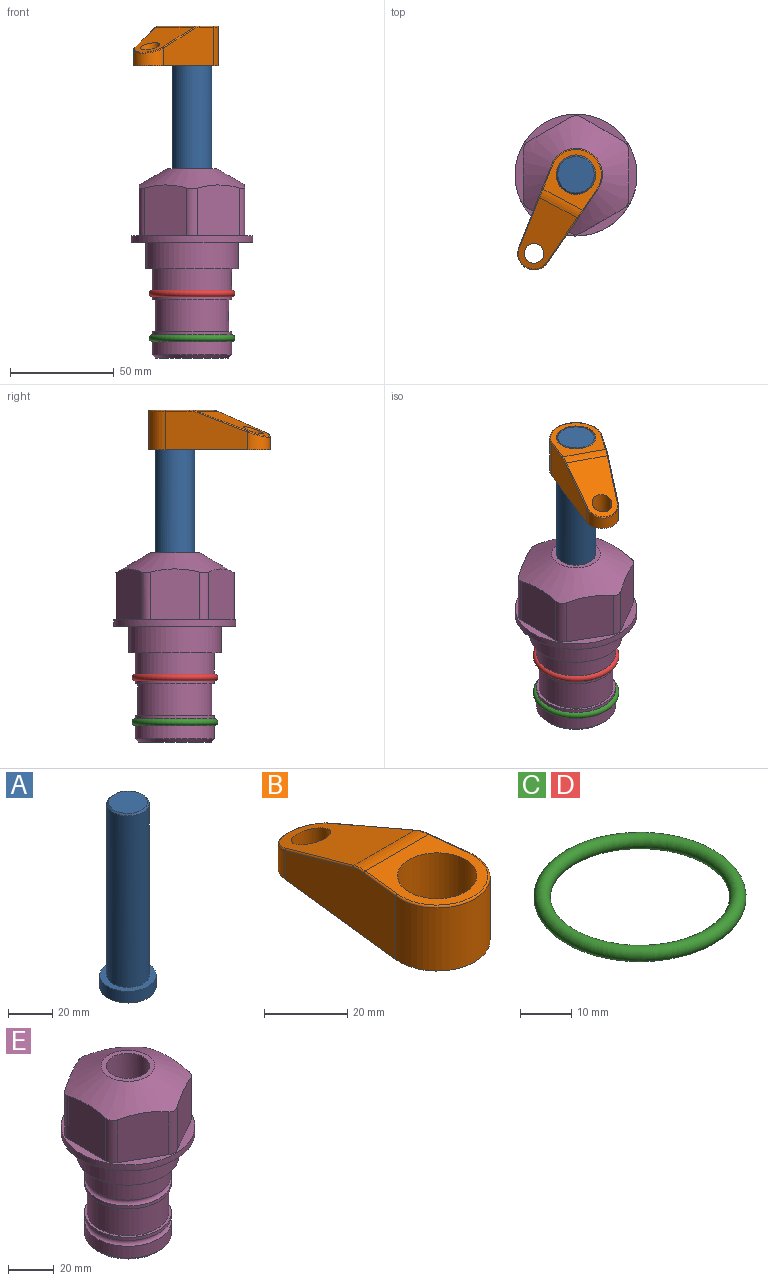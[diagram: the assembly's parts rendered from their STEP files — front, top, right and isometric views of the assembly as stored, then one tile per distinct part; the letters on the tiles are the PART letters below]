
ASSEMBLY  parts=5 mates=3
PART A: 6 faces, bbox 25.4x25.4x101.6 mm
  f0: plane 17.46x17.46mm, normal (0,0,1), area 239.5mm2, adj f5
  f1: plane 25.4x25.4mm, normal (0,0,-1), area 506.7mm2, adj f2
  f2: cylinder r=12.7mm len=25.4mm, axis (0,0,1), area 506.7mm2, adj f1,f3
  f3: plane 25.4x25.4mm, normal (0,0,1), area 221.7mm2, adj f2,f4
  f4: cylinder r=9.53mm len=94.46mm, axis (0,0,1), area 5653mm2, adj f3,f5
  f5: cone r=8.73mm half-angle=45deg, axis (0,0,-1), area 64.4mm2, adj f0,f4
PART B: 44 faces, bbox 27.5x64.5x19.1 mm
  f0: plane 2.3x0.95mm, normal (0,0,-1), area 1mm2, adj f25,f30,f34
  f1: plane 63.5x25.4mm, normal (0,0,-1), area 561.7mm2, adj f2,f3,f4,f5,f6,f7,f19,f20
  f2: cylinder r=12.7mm len=25.4mm, axis (0,0,-1), area 792.2mm2, adj f1,f3,f5,f13
  f3: plane 42.33x18.54mm, normal (0.99,0.11,0), area 647mm2, adj f1,f2,f4,f11,f12,f14
  f4: cylinder r=7.94mm len=15.78mm, axis (0,0,-1), area 158.6mm2, adj f1,f3,f5,f16
  f5: plane 42.33x18.54mm, normal (-0.99,0.11,0), area 647mm2, adj f1,f2,f4,f15,f17,f18
  f6: cylinder r=9.53mm len=19.05mm, axis (0,0,-1), area 1140.1mm2, adj f1,f8
  f7: cylinder r=4.76mm len=10.98mm, axis (0,0,-1), area 276.1mm2, adj f1,f9
  f8: plane 25.83x24.38mm, normal (0,0,1), area 262.2mm2, adj f6,f10,f11,f13,f15
  f9: plane 32.49x20.55mm, normal (0,0.34,0.94), area 489.9mm2, adj f7,f10,f14,f16,f18
  f10: cylinder r=12.7mm len=21.49mm, axis (-1,0,0), area 93.2mm2, adj f8,f9,f12,f17
  f11: cylinder r=0.51mm len=12.34mm, axis (0.11,-0.99,0), area 9.9mm2, adj f3,f8,f12,f13
  f12: bspline ~7.62x1.64mm, area 3.5mm2, adj f3,f10,f11,f14
  f13: torus R=12.19mm, axis (0,0,1), area 33.6mm2, adj f2,f8,f11,f15
  f14: cylinder r=0.51mm len=26.01mm, axis (0.1,-0.93,0.34), area 21.6mm2, adj f3,f9,f12,f16
  f15: cylinder r=0.51mm len=12.34mm, axis (0.11,0.99,0), area 9.9mm2, adj f5,f8,f13,f17
  f16: bspline ~15.78x7.05mm, area 15.7mm2, adj f4,f9,f14,f18
  f17: bspline ~7.62x1.64mm, area 3.5mm2, adj f5,f10,f15,f18
  f18: cylinder r=0.51mm len=26.01mm, axis (0.1,0.93,-0.34), area 21.6mm2, adj f5,f9,f16,f17
  f19: plane 21.6x14.29mm, normal (-0.99,-0.11,0), area 242.6mm2, adj f1,f26,f28,f34,f36,f38
  f20: plane 21.6x14.29mm, normal (0.99,-0.11,0), area 242.6mm2, adj f1,f27,f29,f37,f39,f41
  f21: cylinder r=12.7mm len=14.29mm, axis (0,0,-1), area 173.2mm2, adj f1,f26,f27,f30,f31,f33
  f22: cylinder r=7.94mm len=7.63mm, axis (0,0,-1), area 53.8mm2, adj f1,f28,f29,f42
  f23: plane 2.3x0.95mm, normal (0,0,-1), area 1mm2, adj f25,f33,f37
  f24: plane 17.94x12.32mm, normal (0,-0.34,-0.94), area 191.2mm2, adj f25,f38,f41,f42
  f25: cylinder r=9.53mm len=12.93mm, axis (-1,0,0), area 37.5mm2, adj f0,f23,f24,f31,f36,f39
  f26: cylinder r=1.59mm len=14.29mm, axis (0,0,-1), area 49mm2, adj f1,f19,f21,f32
  f27: cylinder r=1.59mm len=14.29mm, axis (0,0,-1), area 49mm2, adj f1,f20,f21,f35
  f28: cylinder r=1.59mm len=7.28mm, axis (0,0,-1), area 22.1mm2, adj f1,f19,f22,f40
  f29: cylinder r=1.59mm len=7.28mm, axis (0,0,-1), area 22.1mm2, adj f1,f20,f22,f43
  f30: torus R=14.29mm, axis (0,0,1), area 5.8mm2, adj f0,f21,f31,f32
  f31: bspline ~11.06x2.73mm, area 20.8mm2, adj f21,f25,f30,f33
  f32: sphere r=1.59mm, area 5.4mm2, adj f26,f30,f34
  f33: torus R=14.29mm, axis (0,0,1), area 5.8mm2, adj f21,f23,f31,f35
  f34: cylinder r=1.59mm len=1.68mm, axis (-0.11,0.99,0), area 2.4mm2, adj f0,f19,f32,f36
  f35: sphere r=1.59mm, area 5.4mm2, adj f27,f33,f37
  f36: bspline ~5.82x2.33mm, area 7.7mm2, adj f19,f25,f34,f38
  f37: cylinder r=1.59mm len=1.68mm, axis (0.11,0.99,0), area 2.4mm2, adj f20,f23,f35,f39
  f38: cylinder r=1.59mm len=18.33mm, axis (0.1,-0.93,0.34), area 46.7mm2, adj f19,f24,f36,f40
  f39: bspline ~5.82x2.33mm, area 7.7mm2, adj f20,f25,f37,f41
  f40: sphere r=1.59mm, area 3.6mm2, adj f28,f38,f42
  f41: cylinder r=1.59mm len=18.33mm, axis (0.1,0.93,-0.34), area 46.7mm2, adj f20,f24,f39,f43
  f42: bspline ~8.31x1.84mm, area 15.3mm2, adj f22,f24,f40,f43
  f43: sphere r=1.59mm, area 3.6mm2, adj f29,f41,f42
PART C: 1 faces, bbox 44.7x44.7x3.2 mm
  f0: torus R=19.05mm, axis (0,0,1), area 1193.9mm2
PART D: same geometry as C
PART E: 36 faces, bbox 58.7x58.7x91.2 mm
  f0: cylinder r=17.78mm len=35.56mm, axis (0,0,1), area 1670.8mm2, adj f23,f24,f31
  f1: cylinder r=19.05mm len=38.1mm, axis (0,0,1), area 1191.9mm2, adj f26,f27,f30
  f2: plane 58.66x58.66mm, normal (0,0,-1), area 1150.6mm2, adj f3,f28
  f3: cylinder r=29.33mm len=58.66mm, axis (0,0,-1), area 585.1mm2, adj f2,f4
  f4: plane 58.66x58.66mm, normal (0,0,1), area 475.9mm2, adj f3,f5,f6,f7,f8,f9,f10,f11
  f5: plane 24.5x20.32mm, normal (-0.5,0.87,0), area 562.8mm2, adj f4,f15,f16,f17
  f6: plane 24.5x20.32mm, normal (0.5,0.87,0), area 562.8mm2, adj f4,f14,f15,f17
  f7: plane 24.5x23.48mm, normal (1,0,0), area 562.8mm2, adj f4,f13,f14,f17
  f8: plane 24.5x20.32mm, normal (0.5,-0.87,0), area 562.8mm2, adj f4,f12,f13,f17
  f9: plane 24.5x20.32mm, normal (-0.5,-0.87,0), area 562.8mm2, adj f4,f11,f12,f17
  f10: plane 24.5x23.48mm, normal (-1,0,0), area 562.8mm2, adj f4,f11,f16,f17
  f11: cylinder r=5.08mm len=23.01mm, axis (0,0,-1), area 121.2mm2, adj f4,f9,f10,f17
  f12: cylinder r=5.08mm len=23.01mm, axis (0,0,-1), area 121.2mm2, adj f4,f8,f9,f17
  f13: cylinder r=5.08mm len=23.01mm, axis (0,0,-1), area 121.2mm2, adj f4,f7,f8,f17
  f14: cylinder r=5.08mm len=23.01mm, axis (0,0,-1), area 121.2mm2, adj f4,f6,f7,f17
  f15: cylinder r=5.08mm len=23.01mm, axis (0,0,-1), area 121.2mm2, adj f4,f5,f6,f17
  f16: cylinder r=5.08mm len=23.01mm, axis (0,0,-1), area 121.2mm2, adj f4,f5,f10,f17
  f17: cone r=11.73mm half-angle=60deg, axis (0,0,-1), area 2071.8mm2, adj f5,f6,f7,f8,f9,f10,f11,f12
  f18: plane 23.46x23.46mm, normal (0,0,1), area 147.4mm2, adj f17,f35
  f19: plane 34.93x34.93mm, normal (0,0,-1), area 958mm2, adj f29
  f20: cylinder r=19.05mm len=38.1mm, axis (0,0,1), area 760.1mm2, adj f21,f29
  f21: torus R=19.05mm, axis (0,0,1), area 565.3mm2, adj f20,f22
  f22: cylinder r=19.05mm len=38.1mm, axis (0,0,1), area 190mm2, adj f21,f23
  f23: plane 38.1x38.1mm, normal (0,0,1), area 146.9mm2, adj f0,f22
  f24: plane 38.1x38.1mm, normal (0,0,-1), area 146.9mm2, adj f0,f25
  f25: cylinder r=19.05mm len=38.1mm, axis (0,0,1), area 190mm2, adj f24,f26
  f26: torus R=19.05mm, axis (0,0,1), area 565.3mm2, adj f1,f25
  f27: plane 44.45x44.45mm, normal (0,0,-1), area 411.7mm2, adj f1,f28
  f28: cylinder r=22.23mm len=44.45mm, axis (0,0,1), area 1773.5mm2, adj f2,f27
  f29: cone r=19.05mm half-angle=45deg, axis (0,0,1), area 257.5mm2, adj f19,f20
  f30: cylinder r=3.17mm len=6.75mm, axis (-1,0,0), area 128mm2, adj f1,f33
  f31: cylinder r=3.17mm len=6.35mm, axis (-1,0,0), area 102.5mm2, adj f0,f33
  f32: plane 25.4x25.4mm, normal (0,0,1), area 506.7mm2, adj f33
  f33: cylinder r=12.7mm len=66.42mm, axis (0,0,-1), area 5236.2mm2, adj f30,f31,f32,f34
  f34: cone r=9.53mm half-angle=30deg, axis (0,0,-1), area 443.4mm2, adj f33,f35
  f35: cylinder r=9.53mm len=19.05mm, axis (0,0,-1), area 849mm2, adj f18,f34
PLACE A rot(axis=(0,0,-1),118.1deg) t=(0,0,30.48)mm
PLACE B rot(axis=(0,0,1),151.9deg) t=(0,0,85.09)mm
PLACE C t=(0,0,-21.59)mm
PLACE D at identity
PLACE E at identity fixed
MATE fastened C.f0 <-> E.f0  axis (0,0,1) through (0,0,-46.1)mm
MATE cylindrical A.f2 <-> E.f0  axis (0,0,1) through (0,0,56.12)mm
MATE fastened B.f2 <-> A.f2  axis (0,0,1) through (0,0,104.14)mm
